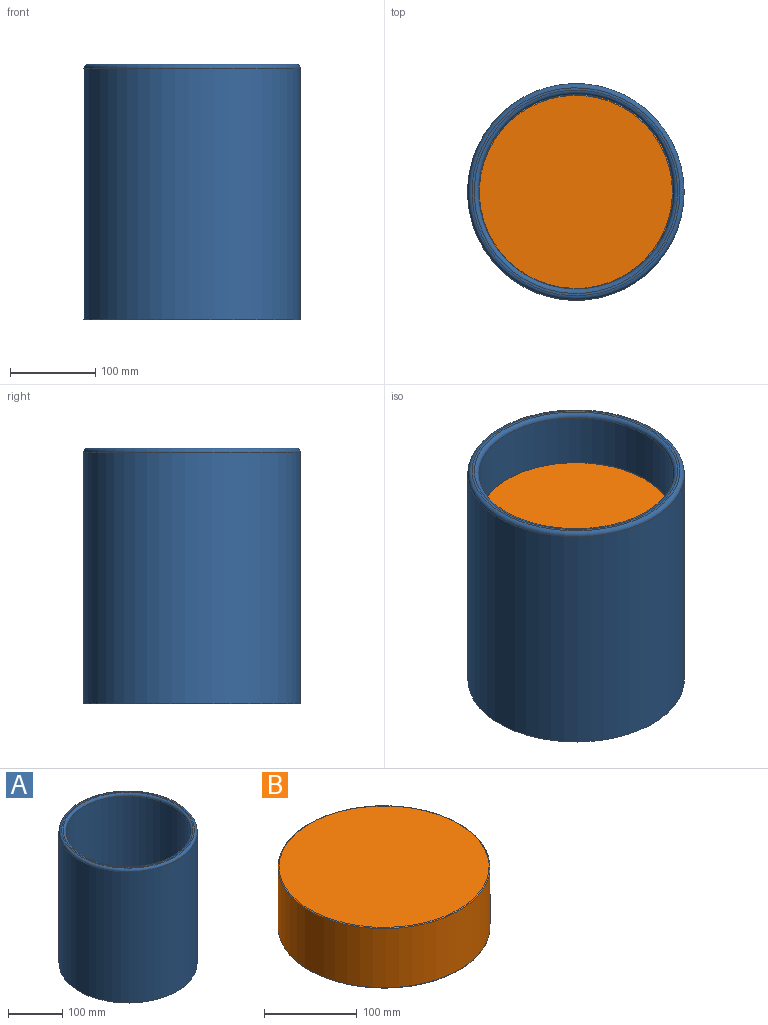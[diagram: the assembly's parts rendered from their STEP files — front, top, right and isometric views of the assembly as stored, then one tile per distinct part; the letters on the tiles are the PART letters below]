
ASSEMBLY  parts=2 mates=1
PART A: 7 faces, bbox 274.9x274.9x300 mm
  f0: cylinder r=114.3mm len=285mm, axis (0,0,-1), area 204677.9mm2, adj f4,f6
  f1: cylinder r=127mm len=295mm, axis (0,0,-1), area 235399.5mm2, adj f3,f5
  f2: plane 244x244mm, normal (0,0,1), area 2046.8mm2, adj f4,f5
  f3: plane 254x254mm, normal (0,0,-1), area 2131.6mm2, adj f1,f6
  f4: torus R=119.3mm, axis (0,0,1), area 5730.1mm2, adj f0,f2
  f5: torus R=122mm, axis (0,0,1), area 6177.5mm2, adj f1,f2
  f6: cone r=124.3mm half-angle=45deg, axis (0,0,-1), area 10600.7mm2, adj f0,f3
PART B: 5 faces, bbox 247.4x247.4x80 mm
  f0: cylinder r=114.3mm len=228.6mm, axis (0,0,-1), area 56017.1mm2, adj f3,f4
  f1: plane 226.6x226.6mm, normal (0,0,1), area 40328.3mm2, adj f3
  f2: plane 226.6x226.6mm, normal (0,0,-1), area 40328.3mm2, adj f4
  f3: torus R=113.3mm, axis (0,0,1), area 1124.5mm2, adj f0,f1
  f4: torus R=113.3mm, axis (0,0,1), area 1124.5mm2, adj f0,f2
PLACE A t=(-431.69,-189.84,-365.81)mm
PLACE B t=(-431.69,-189.84,-214.31)mm
MATE slider B.f0 <-> A.f0  axis (0,0,-1) through (-431.69,-189.84,-213.31)mm
